# Revit family: FantiniCosmi_BIM_AP20068
name_source: partatom
category: Generic Models
units: mm (PartAtom-declared; Revit-internal decimal feet)

## family parameters
Always vertical = Yes
Can host rebar = No
Cut with Voids When Loaded = No
Part Type = Normal
Room Calculation Point = No
Round Connector Dimension = Use Diameter
Shared = No
Work Plane-Based = No

## types (1)
- Standard
    COP totale = 4,3
    Default Elevation = 0 mm  [stored 0 ft]
    Description = ASPIRCOMFORT PRO X 460H
    EER totale = 3,0
    Max Potenza assorbita compressori = 1,15 kW
    Max Potenza assorbita totale = 1,27 kW
    Max Potenza assorbita ventilatori = 0,12 kW
    Max corrente assorbita totale = 5,8 A
    Numero Ventilatori = 2
    Part Number = AP20068
    Portata aria BO / V3 / V2 / V1 = 460 / 400 / 240 / 140 mc/h
    Tensione di alimentazione = 220/1/50  V/ph/Hz

note: [stored X ft] marks values corroborated as IEEE doubles in the binary element streams (Revit-internal decimal feet)

## geometry (parser evidence)
native form markers: Sweep x3
no freeform markers — native parametric forms only
